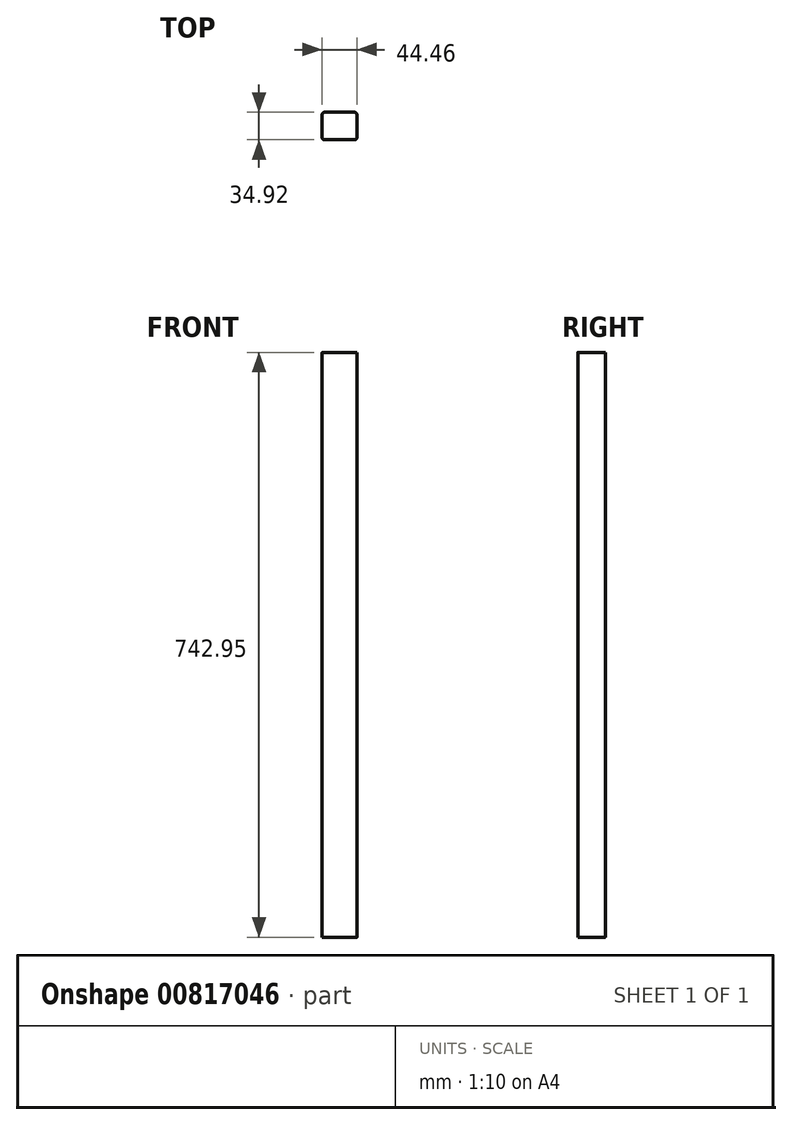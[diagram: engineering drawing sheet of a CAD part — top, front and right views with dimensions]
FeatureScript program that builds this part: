
annotation { "Feature Type Name" : "Feature", "Feature Type Description" : "" }
export const myFeature = defineFeature(function(context is Context, id is Id, definition is map)
    precondition{}
    {
        {
            var Q0;
            Q0=qCreatedBy(makeId("Top.planeOp"),FACE);
            var sketch = newSketch(context, id + "F0", { "sketchPlane" : qUnion([Q0])});
            skLineSegment(sketch, "E0.bottom", {"start": v(22.23, 17.46) * mm, "end": v(-22.23, 17.46) * mm});
            skLineSegment(sketch, "E0.top", {"start": v(22.23, -17.46) * mm, "end": v(-22.23, -17.46) * mm});
            skLineSegment(sketch, "E0.left", {"start": v(22.23, 17.46) * mm, "end": v(22.23, -17.46) * mm});
            skLineSegment(sketch, "E0.right", {"start": v(-22.23, 17.46) * mm, "end": v(-22.23, -17.46) * mm});
            skPoint(sketch, "E0.middle", {"position": v(0, 0) * mm});
            skSolve(sketch);
        }
        {
            var Q0;
            Q0 = qSketchRegion(id + "F0", true);
            extrude(context, id + "F1", {"entities" : qUnion([Q0]), "depth" : 742.95 * mm, "offsetDistance" : 25.4 * mm});
        }
        {
            var Q0;
            Q0=makeQuery(id+"F1.opExtrude","SWEPT_EDGE",EDGE,{"disambiguationData":[OSD([sQuery(id+"F0.wireOp",EDGE,"E0.top"),sQuery(id+"F0.wireOp",EDGE,"E0.left")])]});
            var Q1;
            Q1=makeQuery(id+"F1.opExtrude","SWEPT_EDGE",EDGE,{"disambiguationData":[OSD([sQuery(id+"F0.wireOp",EDGE,"E0.top"),sQuery(id+"F0.wireOp",EDGE,"E0.right")])]});
            fillet(context, id + "F2", {"entities" : qUnion([Q0, Q1]), "radius" : 3.17 * mm, "tangentPropagation" : true, "allowEdgeOverflow" : false});
        }
        {
            var Q0;
            Q0=makeQuery(id+"F1.opExtrude","SWEPT_EDGE",EDGE,{"disambiguationData":[OSD([sQuery(id+"F0.wireOp",EDGE,"E0.bottom"),sQuery(id+"F0.wireOp",EDGE,"E0.left")])]});
            var Q1;
            Q1=makeQuery(id+"F1.opExtrude","SWEPT_EDGE",EDGE,{"disambiguationData":[OSD([sQuery(id+"F0.wireOp",EDGE,"E0.bottom"),sQuery(id+"F0.wireOp",EDGE,"E0.right")])]});
            fillet(context, id + "F3", {"entities" : qUnion([Q0, Q1]), "radius" : 3.17 * mm, "tangentPropagation" : true, "allowEdgeOverflow" : false});
        }
    });
